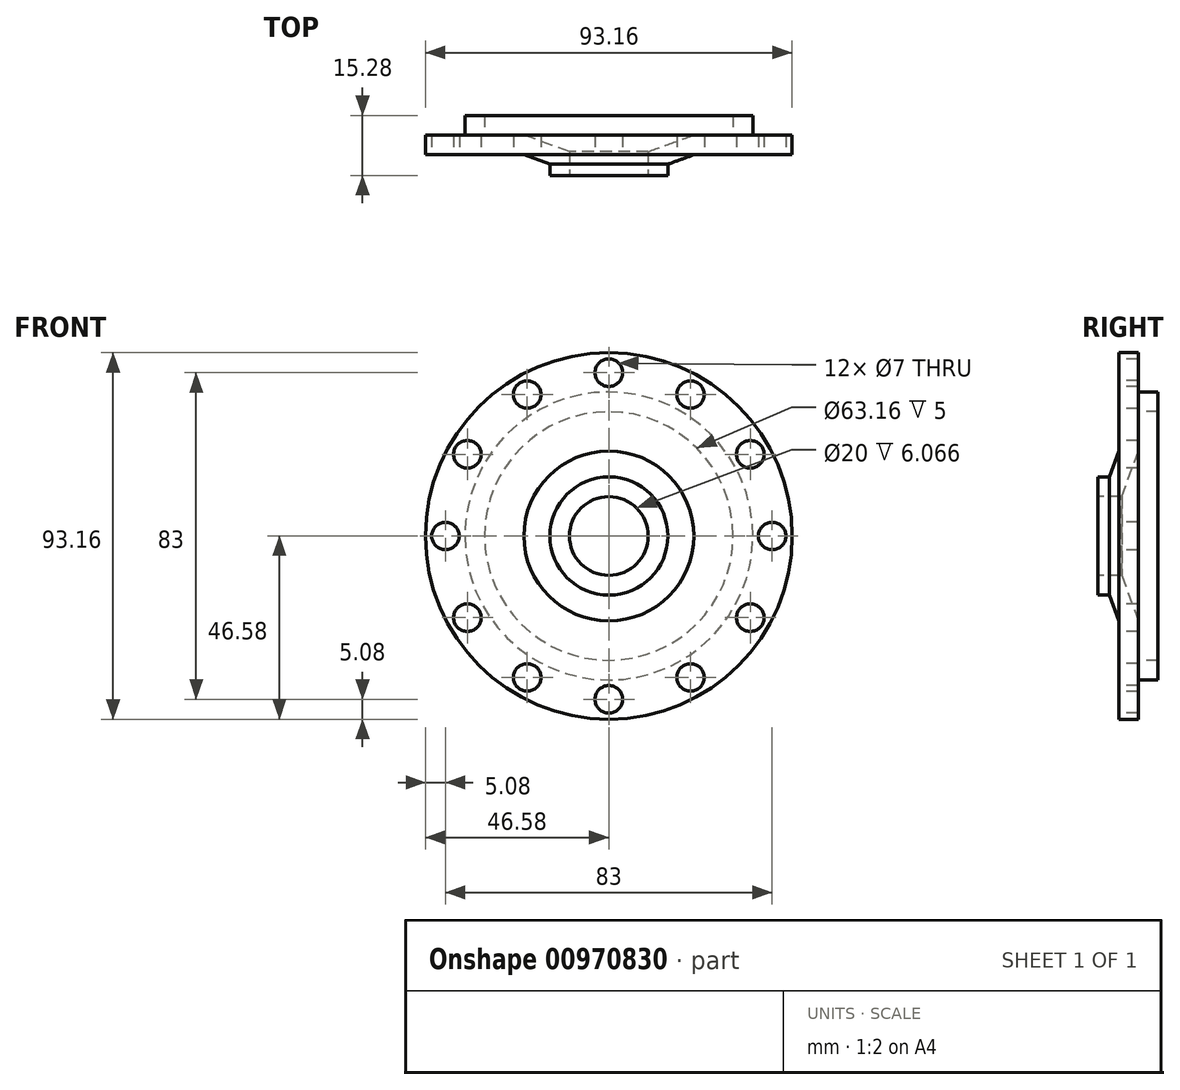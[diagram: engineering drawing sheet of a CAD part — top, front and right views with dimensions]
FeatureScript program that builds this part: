
annotation { "Feature Type Name" : "Feature", "Feature Type Description" : "" }
export const myFeature = defineFeature(function(context is Context, id is Id, definition is map)
    precondition{}
    {
        {
            var Q0;
            Q0=qCreatedBy(makeId("Top.planeOp"),FACE);
            var sketch = newSketch(context, id + "F0", { "sketchPlane" : qUnion([Q0])});
            skLineSegment(sketch, "E0", {"start": v(0, 23.1) * mm, "end": v(0, -24.52) * mm, "construction": true});
            skLineSegment(sketch, "E1", {"start": v(21.58, 10.28) * mm, "end": v(31.58, 10.28) * mm});
            skLineSegment(sketch, "E2", {"start": v(31.58, 10.28) * mm, "end": v(31.58, 15.28) * mm});
            skLineSegment(sketch, "E3", {"start": v(31.58, 15.28) * mm, "end": v(36.58, 15.28) * mm});
            skLineSegment(sketch, "E4", {"start": v(36.58, 15.28) * mm, "end": v(36.58, 10.28) * mm});
            skLineSegment(sketch, "E5", {"start": v(36.58, 10.28) * mm, "end": v(46.58, 10.28) * mm});
            skLineSegment(sketch, "E6", {"start": v(46.58, 10.28) * mm, "end": v(46.58, 5.28) * mm});
            skLineSegment(sketch, "E7", {"start": v(46.58, 5.28) * mm, "end": v(21.58, 5.28) * mm});
            skLineSegment(sketch, "E8", {"start": v(21.58, 5.28) * mm, "end": v(15, 2.89) * mm});
            skLineSegment(sketch, "E9", {"start": v(15, 2.89) * mm, "end": v(15, 0) * mm});
            skLineSegment(sketch, "E10", {"start": v(10, 0) * mm, "end": v(10, 6.07) * mm});
            skLineSegment(sketch, "E11", {"start": v(21.58, 10.28) * mm, "end": v(10, 6.07) * mm});
            skLineSegment(sketch, "E12", {"start": v(15, 0) * mm, "end": v(10, 0) * mm});
            skSolve(sketch);
        }
        {
            var Q0;
            Q0=qCreatedBy(makeId("Front.planeOp"),FACE);
            var sketch = newSketch(context, id + "F1", { "sketchPlane" : qUnion([Q0])});
            skCircle(sketch, "E13", {"center": v(0, 0) * mm, "radius": 12.5 * mm});
            skSolve(sketch);
        }
        {
            var Q0;
            Q0=makeQuery(id+"F0.imprint","IMPRINT",FACE,{"disambiguationData":[TD([[makeQuery(id+"F0.imprint","IMPRINT",EDGE,{"derivedFrom":sQuery(id+"F0.wireOp",EDGE,"E1")}),-1.0]])]});
            var Q1;
            Q1=sQuery(id+"F1.wireOp",EDGE,"E13");
            sweep(context, id + "F2", {"profiles" : qUnion([Q0]), "path" : qUnion([Q1])});
        }
        {
            var Q0;
            Q0=qCreatedBy(makeId("Front.planeOp"),FACE);
            var sketch = newSketch(context, id + "F3", { "sketchPlane" : qUnion([Q0])});
            skCircle(sketch, "E14.0", {"center": v(0, 0) * mm, "radius": 46.58 * mm});
            skCircle(sketch, "E15", {"center": v(0, 41.5) * mm, "radius": 3.5 * mm});
            skCircle(sketch, "E16.1.0", {"center": v(-20.75, 35.94) * mm, "radius": 3.5 * mm});
            skCircle(sketch, "E16.2.0", {"center": v(-35.94, 20.75) * mm, "radius": 3.5 * mm});
            skCircle(sketch, "E16.3.0", {"center": v(-41.5, 0) * mm, "radius": 3.5 * mm});
            skCircle(sketch, "E16.4.0", {"center": v(-35.94, -20.75) * mm, "radius": 3.5 * mm});
            skCircle(sketch, "E16.5.0", {"center": v(-20.75, -35.94) * mm, "radius": 3.5 * mm});
            skCircle(sketch, "E16.6.0", {"center": v(0, -41.5) * mm, "radius": 3.5 * mm});
            skCircle(sketch, "E16.7.0", {"center": v(20.75, -35.94) * mm, "radius": 3.5 * mm});
            skCircle(sketch, "E16.8.0", {"center": v(35.94, -20.75) * mm, "radius": 3.5 * mm});
            skCircle(sketch, "E16.9.0", {"center": v(41.5, 0) * mm, "radius": 3.5 * mm});
            skCircle(sketch, "E16.10.0", {"center": v(35.94, 20.75) * mm, "radius": 3.5 * mm});
            skCircle(sketch, "E16.11.0", {"center": v(20.75, 35.94) * mm, "radius": 3.5 * mm});
            skSolve(sketch);
        }
        {
            var Q0;
            Q0=makeQuery(id+"F3.imprint","IMPRINT",FACE,{"disambiguationData":[TD([[makeQuery(id+"F3.imprint","IMPRINT",EDGE,{"derivedFrom":sQuery(id+"F3.wireOp",EDGE,"E15")}),1.0]])]});
            var Q1;
            Q1=sQuery(id+"F3.wireOp",EDGE,"E16.9.0");
            var Q2;
            Q2=sQuery(id+"F3.wireOp",EDGE,"E16.10.0");
            var Q3;
            Q3=sQuery(id+"F3.wireOp",EDGE,"E16.11.0");
            var Q4;
            Q4=sQuery(id+"F3.wireOp",EDGE,"E15");
            var Q5;
            Q5=sQuery(id+"F3.wireOp",EDGE,"E16.1.0");
            var Q6;
            Q6=sQuery(id+"F3.wireOp",EDGE,"E16.2.0");
            var Q7;
            Q7=sQuery(id+"F3.wireOp",EDGE,"E16.3.0");
            var Q8;
            Q8=sQuery(id+"F3.wireOp",EDGE,"E16.4.0");
            var Q9;
            Q9=sQuery(id+"F3.wireOp",EDGE,"E16.5.0");
            var Q10;
            Q10=sQuery(id+"F3.wireOp",EDGE,"E16.6.0");
            var Q11;
            Q11=sQuery(id+"F3.wireOp",EDGE,"E16.7.0");
            var Q12;
            Q12=sQuery(id+"F3.wireOp",EDGE,"E16.8.0");
            extrude(context, id + "F4", {"entities" : qUnion([Q0]), "operationType" : NewBodyOperationType.REMOVE, "surfaceEntities" : qUnion([Q1, Q2, Q3, Q4, Q5, Q6, Q7, Q8, Q9, Q10, Q11, Q12]), "endBound" : BoundingType.THROUGH_ALL, "oppositeDirection" : true, "depth" : 25 * mm, "offsetDistance" : 25 * mm});
        }
        {
            var Q0;
            Q0=makeQuery(id+"F3.imprint","IMPRINT",FACE,{"disambiguationData":[TD([[makeQuery(id+"F3.imprint","IMPRINT",EDGE,{"derivedFrom":sQuery(id+"F3.wireOp",EDGE,"E16.1.0")}),1.0]])]});
            var Q1;
            Q1=makeQuery(id+"F3.imprint","IMPRINT",FACE,{"disambiguationData":[TD([[makeQuery(id+"F3.imprint","IMPRINT",EDGE,{"derivedFrom":sQuery(id+"F3.wireOp",EDGE,"E16.2.0")}),1.0]])]});
            var Q2;
            Q2=makeQuery(id+"F3.imprint","IMPRINT",FACE,{"disambiguationData":[TD([[makeQuery(id+"F3.imprint","IMPRINT",EDGE,{"derivedFrom":sQuery(id+"F3.wireOp",EDGE,"E16.3.0")}),1.0]])]});
            var Q3;
            Q3=makeQuery(id+"F3.imprint","IMPRINT",FACE,{"disambiguationData":[TD([[makeQuery(id+"F3.imprint","IMPRINT",EDGE,{"derivedFrom":sQuery(id+"F3.wireOp",EDGE,"E16.4.0")}),1.0]])]});
            var Q4;
            Q4=makeQuery(id+"F3.imprint","IMPRINT",FACE,{"disambiguationData":[TD([[makeQuery(id+"F3.imprint","IMPRINT",EDGE,{"derivedFrom":sQuery(id+"F3.wireOp",EDGE,"E16.5.0")}),1.0]])]});
            var Q5;
            Q5=makeQuery(id+"F3.imprint","IMPRINT",FACE,{"disambiguationData":[TD([[makeQuery(id+"F3.imprint","IMPRINT",EDGE,{"derivedFrom":sQuery(id+"F3.wireOp",EDGE,"E16.6.0")}),1.0]])]});
            var Q6;
            Q6=makeQuery(id+"F3.imprint","IMPRINT",FACE,{"disambiguationData":[TD([[makeQuery(id+"F3.imprint","IMPRINT",EDGE,{"derivedFrom":sQuery(id+"F3.wireOp",EDGE,"E16.7.0")}),1.0]])]});
            var Q7;
            Q7=makeQuery(id+"F3.imprint","IMPRINT",FACE,{"disambiguationData":[TD([[makeQuery(id+"F3.imprint","IMPRINT",EDGE,{"derivedFrom":sQuery(id+"F3.wireOp",EDGE,"E16.8.0")}),1.0]])]});
            var Q8;
            Q8=makeQuery(id+"F3.imprint","IMPRINT",FACE,{"disambiguationData":[TD([[makeQuery(id+"F3.imprint","IMPRINT",EDGE,{"derivedFrom":sQuery(id+"F3.wireOp",EDGE,"E16.9.0")}),1.0]])]});
            var Q9;
            Q9=makeQuery(id+"F3.imprint","IMPRINT",FACE,{"disambiguationData":[TD([[makeQuery(id+"F3.imprint","IMPRINT",EDGE,{"derivedFrom":sQuery(id+"F3.wireOp",EDGE,"E16.10.0")}),1.0]])]});
            var Q10;
            Q10=makeQuery(id+"F3.imprint","IMPRINT",FACE,{"disambiguationData":[TD([[makeQuery(id+"F3.imprint","IMPRINT",EDGE,{"derivedFrom":sQuery(id+"F3.wireOp",EDGE,"E16.11.0")}),1.0]])]});
            var Q11;
            Q11=makeQuery(id+"F3.imprint","IMPRINT",FACE,{"disambiguationData":[TD([[makeQuery(id+"F3.imprint","IMPRINT",EDGE,{"derivedFrom":sQuery(id+"F3.wireOp",EDGE,"E15")}),1.0]])]});
            var Q12;
            Q12=sQuery(id+"F3.wireOp",EDGE,"E16.11.0");
            var Q13;
            Q13=sQuery(id+"F3.wireOp",EDGE,"E16.10.0");
            var Q14;
            Q14=sQuery(id+"F3.wireOp",EDGE,"E16.9.0");
            var Q15;
            Q15=sQuery(id+"F3.wireOp",EDGE,"E16.8.0");
            var Q16;
            Q16=sQuery(id+"F3.wireOp",EDGE,"E16.7.0");
            var Q17;
            Q17=sQuery(id+"F3.wireOp",EDGE,"E16.6.0");
            var Q18;
            Q18=sQuery(id+"F3.wireOp",EDGE,"E16.5.0");
            var Q19;
            Q19=sQuery(id+"F3.wireOp",EDGE,"E16.4.0");
            var Q20;
            Q20=sQuery(id+"F3.wireOp",EDGE,"E16.3.0");
            var Q21;
            Q21=sQuery(id+"F3.wireOp",EDGE,"E16.2.0");
            var Q22;
            Q22=sQuery(id+"F3.wireOp",EDGE,"E16.1.0");
            extrude(context, id + "F5", {"entities" : qUnion([Q0, Q1, Q2, Q3, Q4, Q5, Q6, Q7, Q8, Q9, Q10, Q11]), "operationType" : NewBodyOperationType.REMOVE, "surfaceEntities" : qUnion([Q12, Q13, Q14, Q15, Q16, Q17, Q18, Q19, Q20, Q21, Q22]), "oppositeDirection" : true, "depth" : 25 * mm, "offsetDistance" : 25 * mm});
        }
    });
